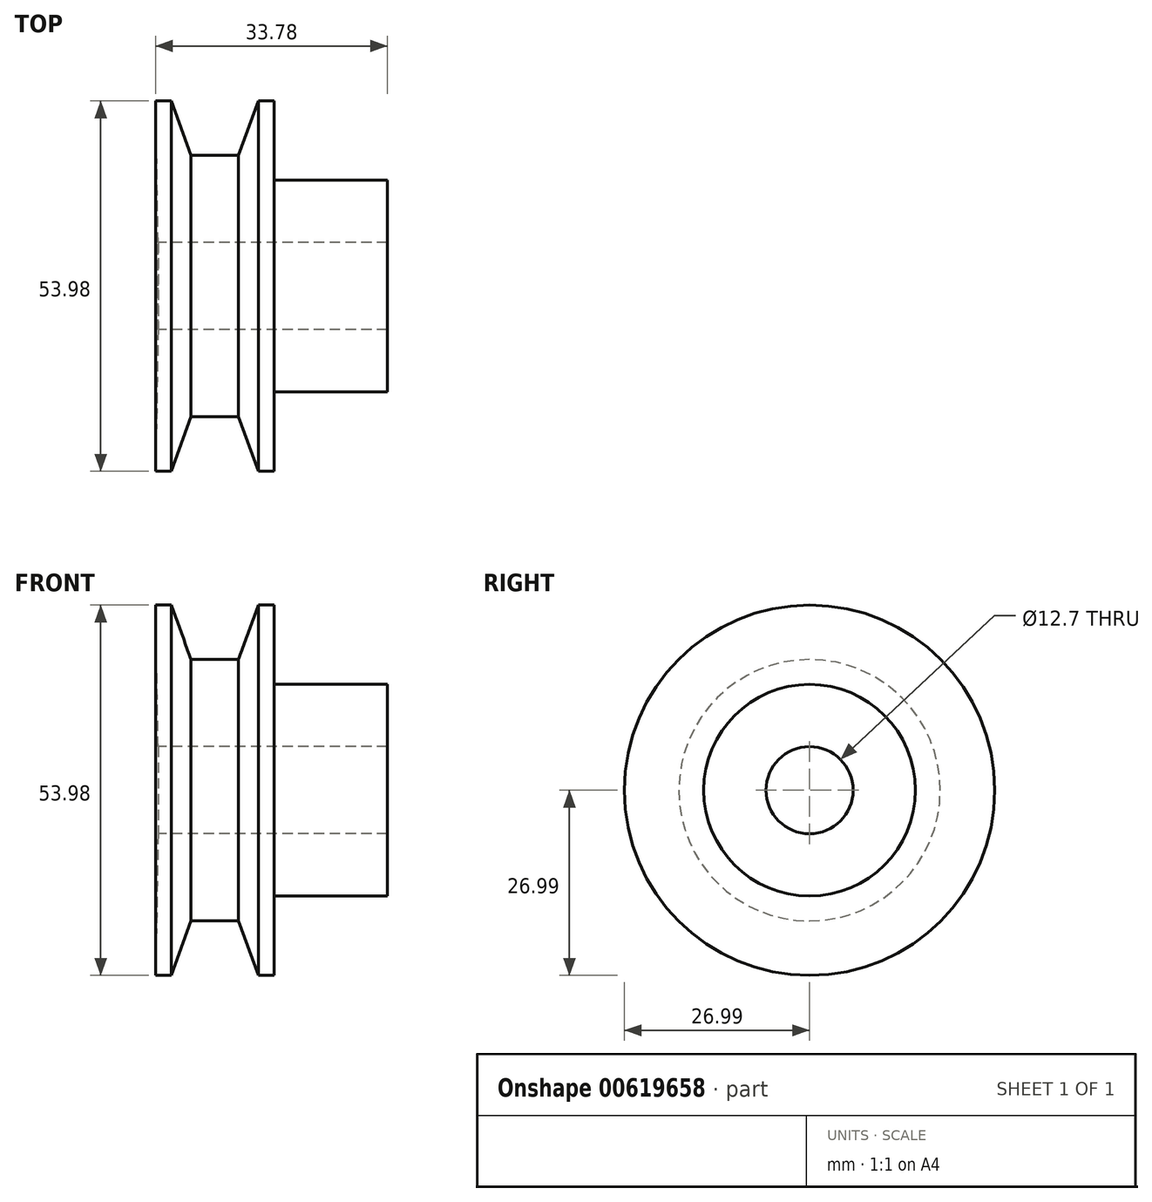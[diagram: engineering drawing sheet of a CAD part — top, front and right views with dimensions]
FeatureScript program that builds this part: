
annotation { "Feature Type Name" : "Feature", "Feature Type Description" : "" }
export const myFeature = defineFeature(function(context is Context, id is Id, definition is map)
    precondition{}
    {
        {
            var Q0;
            Q0=qCreatedBy(makeId("Front.planeOp"),FACE);
            var sketch = newSketch(context, id + "F0", { "sketchPlane" : qUnion([Q0])});
            skLineSegment(sketch, "E0", {"start": v(8.63, 26.99) * mm, "end": v(6.35, 26.99) * mm});
            skLineSegment(sketch, "E1", {"start": v(6.35, 26.99) * mm, "end": v(3.46, 19.05) * mm});
            skLineSegment(sketch, "E2", {"start": v(3.46, 19.05) * mm, "end": v(0, 19.05) * mm});
            skLineSegment(sketch, "E3", {"start": v(0, 19.42) * mm, "end": v(0, -9.12) * mm, "construction": true});
            skLineSegment(sketch, "E4", {"start": v(8.63, 26.99) * mm, "end": v(8.63, 15.43) * mm});
            skLineSegment(sketch, "E5", {"start": v(8.63, 15.43) * mm, "end": v(25.15, 15.43) * mm});
            skLineSegment(sketch, "E6", {"start": v(25.15, 15.43) * mm, "end": v(25.15, 6.35) * mm});
            skLineSegment(sketch, "E7", {"start": v(25.15, 6.35) * mm, "end": v(0, 6.35) * mm});
            skLineSegment(sketch, "E8", {"start": v(0, 6.35) * mm, "end": v(-8.27, 6.35) * mm});
            skLineSegment(sketch, "E9.MirrorCS", {"start": v(-3.46, 19.05) * mm, "end": v(0, 19.05) * mm});
            skLineSegment(sketch, "E10.MirrorCS", {"start": v(-6.35, 26.99) * mm, "end": v(-3.46, 19.05) * mm});
            skLineSegment(sketch, "E11.MirrorCS", {"start": v(-8.63, 26.99) * mm, "end": v(-6.35, 26.99) * mm});
            skLineSegment(sketch, "E12", {"start": v(-8.63, 26.99) * mm, "end": v(-8.27, 6.35) * mm});
            skLineSegment(sketch, "E13", {"start": v(-23.02, 0) * mm, "end": v(34.4, 0) * mm, "construction": true});
            skSolve(sketch);
        }
        {
            var Q0;
            Q0=makeQuery(id+"F0.imprint","IMPRINT",FACE,{"disambiguationData":[TD([[makeQuery(id+"F0.imprint","IMPRINT",EDGE,{"derivedFrom":sQuery(id+"F0.wireOp",EDGE,"E0")}),1.0]])]});
            var Q1;
            Q1=sQuery(id+"F0.wireOp",EDGE,"E13");
            revolve(context, id + "F1", {"entities" : qUnion([Q0]), "axis" : qUnion([Q1]), "revolveType" : RevolveType.FULL});
        }
    });
